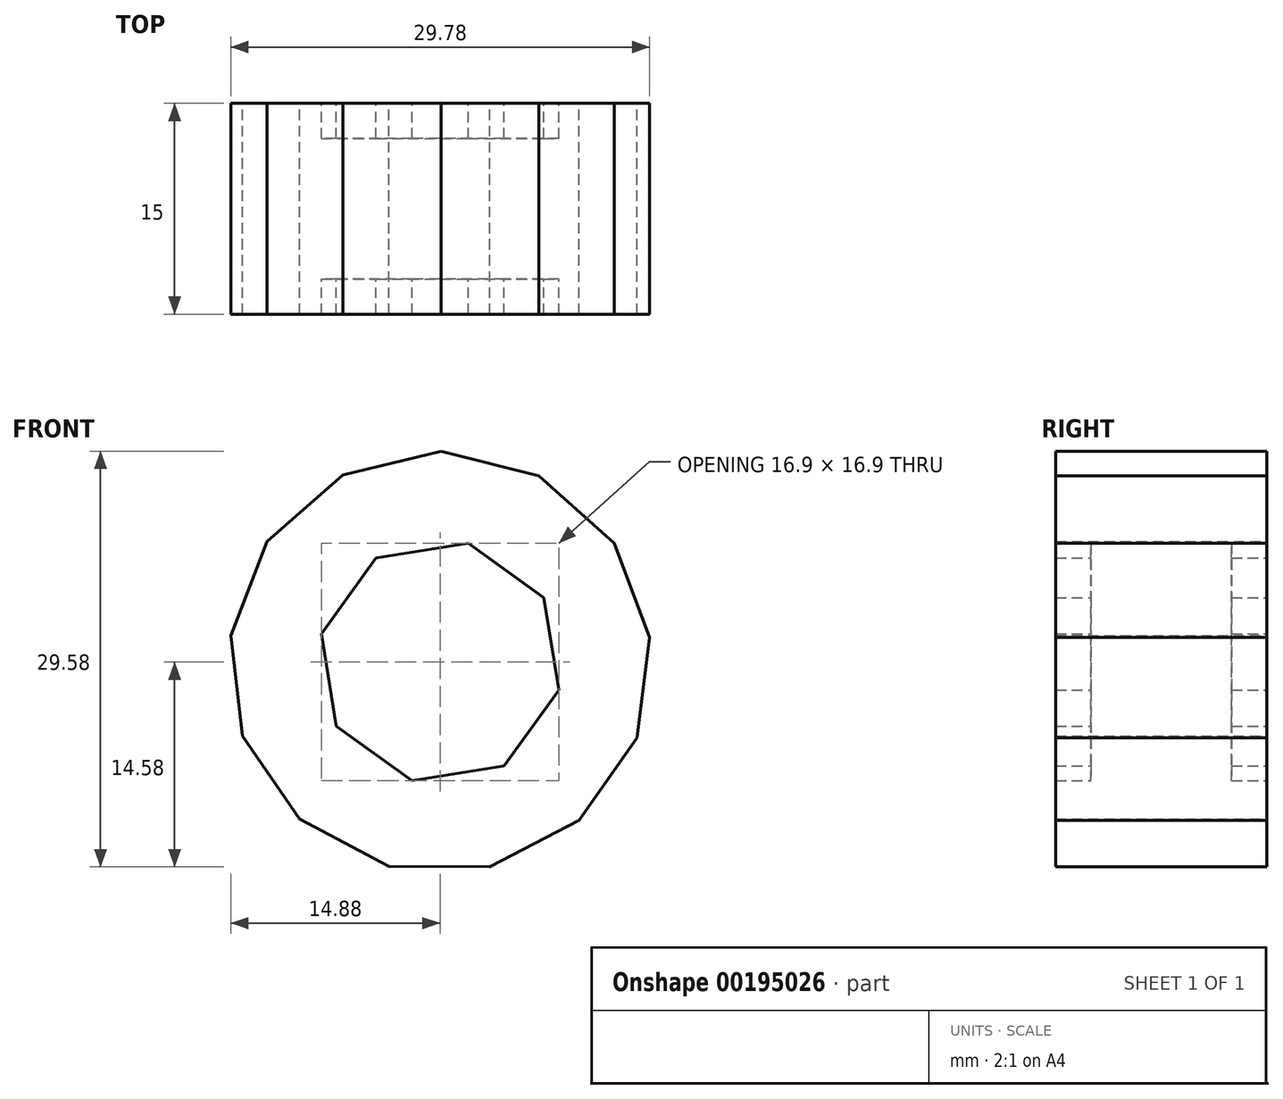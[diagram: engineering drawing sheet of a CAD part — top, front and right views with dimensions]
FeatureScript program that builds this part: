
annotation { "Feature Type Name" : "Feature", "Feature Type Description" : "" }
export const myFeature = defineFeature(function(context is Context, id is Id, definition is map)
    precondition{}
    {
        {
            var Q0;
            Q0=qCreatedBy(makeId("Front.planeOp"),FACE);
            var sketch = newSketch(context, id + "F0", { "sketchPlane" : qUnion([Q0])});
            skLineSegment(sketch, "E0.0", {"start": v(9.9, -11.27) * mm, "end": v(3.52, -14.58) * mm});
            skLineSegment(sketch, "E0.1", {"start": v(3.52, -14.58) * mm, "end": v(-3.66, -14.55) * mm});
            skLineSegment(sketch, "E0.2", {"start": v(-3.66, -14.55) * mm, "end": v(-10, -11.18) * mm});
            skLineSegment(sketch, "E0.3", {"start": v(-10, -11.18) * mm, "end": v(-14.05, -5.25) * mm});
            skLineSegment(sketch, "E0.4", {"start": v(-14.05, -5.25) * mm, "end": v(-14.88, 1.88) * mm});
            skLineSegment(sketch, "E0.5", {"start": v(-14.88, 1.88) * mm, "end": v(-12.3, 8.58) * mm});
            skLineSegment(sketch, "E0.6", {"start": v(-12.3, 8.58) * mm, "end": v(-6.9, 13.31) * mm});
            skLineSegment(sketch, "E0.7", {"start": v(-6.9, 13.31) * mm, "end": v(0.07, 15) * mm});
            skLineSegment(sketch, "E0.8", {"start": v(0.07, 15) * mm, "end": v(7.03, 13.25) * mm});
            skLineSegment(sketch, "E0.9", {"start": v(7.03, 13.25) * mm, "end": v(12.38, 8.46) * mm});
            skLineSegment(sketch, "E0.10", {"start": v(12.38, 8.46) * mm, "end": v(14.9, 1.74) * mm});
            skLineSegment(sketch, "E0.11", {"start": v(14.9, 1.74) * mm, "end": v(14, -5.39) * mm});
            skLineSegment(sketch, "E0.12", {"start": v(14, -5.39) * mm, "end": v(9.9, -11.27) * mm});
            skLineSegment(sketch, "E1.0", {"start": v(4.56, -7.39) * mm, "end": v(-2, -8.45) * mm});
            skLineSegment(sketch, "E1.1", {"start": v(-2, -8.45) * mm, "end": v(-7.39, -4.56) * mm});
            skLineSegment(sketch, "E1.2", {"start": v(-7.39, -4.56) * mm, "end": v(-8.45, 2) * mm});
            skLineSegment(sketch, "E1.3", {"start": v(-8.45, 2) * mm, "end": v(-4.56, 7.39) * mm});
            skLineSegment(sketch, "E1.4", {"start": v(-4.56, 7.39) * mm, "end": v(2, 8.45) * mm});
            skLineSegment(sketch, "E1.5", {"start": v(2, 8.45) * mm, "end": v(7.39, 4.56) * mm});
            skLineSegment(sketch, "E1.6", {"start": v(7.39, 4.56) * mm, "end": v(8.45, -2) * mm});
            skLineSegment(sketch, "E1.7", {"start": v(8.45, -2) * mm, "end": v(4.56, -7.39) * mm});
            skSolve(sketch);
        }
        {
            var Q0;
            Q0=makeQuery(id+"F0.imprint","IMPRINT",FACE,{"disambiguationData":[TD([[makeQuery(id+"F0.imprint","IMPRINT",EDGE,{"derivedFrom":sQuery(id+"F0.wireOp",EDGE,"E0.0")}),-1.0]])]});
            extrude(context, id + "F1", {"entities" : qUnion([Q0]), "endBound" : BoundingType.SYMMETRIC, "depth" : 15 * mm});
        }
        {
            var Q0;
            Q0=makeQuery(id+"F0.imprint","IMPRINT",FACE,{"disambiguationData":[TD([[makeQuery(id+"F0.imprint","IMPRINT",EDGE,{"derivedFrom":sQuery(id+"F0.wireOp",EDGE,"E1.0")}),-1.0]])]});
            extrude(context, id + "F2", {"entities" : qUnion([Q0]), "operationType" : NewBodyOperationType.ADD, "endBound" : BoundingType.SYMMETRIC, "depth" : 10 * mm});
        }
    });
